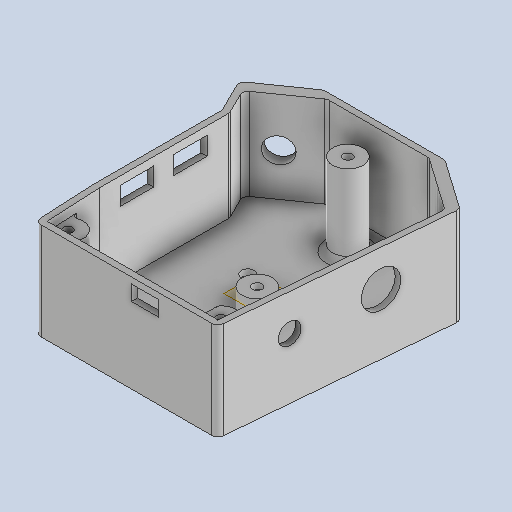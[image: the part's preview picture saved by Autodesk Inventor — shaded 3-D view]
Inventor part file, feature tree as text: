
AUTODESK INVENTOR PART (.ipt)
format: ipt  version: 2025.1 (Build 291241000, 241)  size: 480,256 bytes
history: native  units: mm
features: sketch x12, extrude x10, reference x8, other x4, fillet x3, hole x2, projected_geometry x2, shell x1, mirror x1, plane x1
ambient origin geometry x8: Origin, YZ Plane, XZ Plane, XY Plane, X Axis, Y Axis, Z Axis, Center Point
bodies: Volumenkörper1 (feature_tree)
feature tree (44):
  extrude  "Extrusion1"  Depth=20.0mm
  shell  "Wandung1"  Thickness=20.0mm
  extrude  "Extrusion6"  Depth=25.307274mm
  hole  "Bohrung1"  [1 undecoded]
  extrude  "Extrusion5"  Depth=2.0mm
  mirror  "Spiegeln1"
  extrude  "Extrusion4"  Depth=2.0mm
  extrude  "Extrusion7"  Depth=20.0mm
  extrude  "Extrusion8"  Depth=22.0mm
  plane  "Arbeitsebene1"
  extrude  "Extrusion9"  TaperAngle=0.0deg  [1 undecoded]
  hole  "Bohrung3"  [1 undecoded]
  extrude  "Extrusion10"  Depth=5.0mm
  extrude  "Extrusion11"  Depth=5.0mm
  extrude  "Extrusion12"  Depth=30.0mm TaperAngle=0.0deg
  fillet  "Rundung1"  Radius=0.5mm
  fillet  "Rundung2"  Radius=0.5mm
  fillet  "Rundung3"  Radius=30.1mm
  sketch  "Skizze1"  dims[d2=40.0mm d3=20.0mm d4=20.0mm]
  sketch  "Skizze2"  dims[d5=25.307274mm d6=25.307274mm]
  sketch  "Skizze6"  dims[d7=85.0mm d8=60.0mm]
  sketch  "Skizze7"  dims[d9=32.0mm d10=0.0mm d11=2.0mm]
  sketch  "Skizze8"  dims[d12=8.3mm d13=8.0mm d14=4.0mm d15=2.0mm d16=90.0deg d17=11.8mm d18=20.594885mm d40=12.0mm]
  projected_geometry  "Projizierte Kontur1"
  sketch  "Skizze9"  dims[d41=7.0mm d42=20.0mm]
  sketch  "Skizze10"  dims[d43=24.0mm d44=22.0mm]
  reference  "Referenz1"
  reference  "Referenz2"
  reference  "Referenz3"
  reference  "Referenz4"
  reference  "Referenz5"
  reference  "Referenz6"
  sketch  "Skizze11"  dims[d45=7.0mm d46=0.0mm]
  reference  "Referenz7"
  sketch  "Skizze13"  dims[d47=42.6mm d48=20.0mm]
  reference  "Referenz9"
  sketch  "Skizze14"  dims[d49=31.0mm d50=5.0mm]
  sketch  "Skizze15"  dims[d51=10.0mm d52=5.0mm d53=10.0mm]
  projected_geometry  "Projizierte Kontur2"
  sketch  "Skizze16"  dims[d54=7.5mm d57=30.0mm d58=0.0mm d59=0.5mm d60=0.5mm d61=30.1mm d62=5.7mm d63=3.5mm d64=3.5mm d65=32.0mm d66=0.0mm d67=10.0mm d68=3.2mm d69=9.0mm d70=0.0mm d71=0.5mm d72=9.0mm d73=0.0mm d74=10.0mm d75=3.2mm d76=-2.0mm d77=5.3mm d78=5.3mm d79=0.0mm d80=0.0mm d88=4.2mm d89=6.0mm d90=4.0mm d91=2.0mm d92=90.0deg d93=8.0mm d94=20.594885mm d95=10.0mm d96=10.0mm d97=3.0mm d98=27.0mm d99=0.0mm d100=3.0mm d101=10.0mm d102=6.0mm d103=25.2mm d104=3.0mm d105=10.0mm d106=25.2mm d107=27.0mm d108=0.0mm d109=4.0mm d110=10.0mm d111=6.0mm d112=27.0mm d113=0.0mm d114=1.5mm d115=2.0mm d116=2.0mm]
  other  "<userpath>\OneDrive\Documents\Projekte\Macrolampe\CAD\Baugruppen\Macrolight.iam"
  other  "Macrolight.iam"
  other  "Platine:1"
  other  "hotshouh mount:2"
note: 3 required parameter values undecoded (feature->parameter linkage not recoverable at this tier; creation-order binding heuristic only, values carry confidence <= 0.55)
